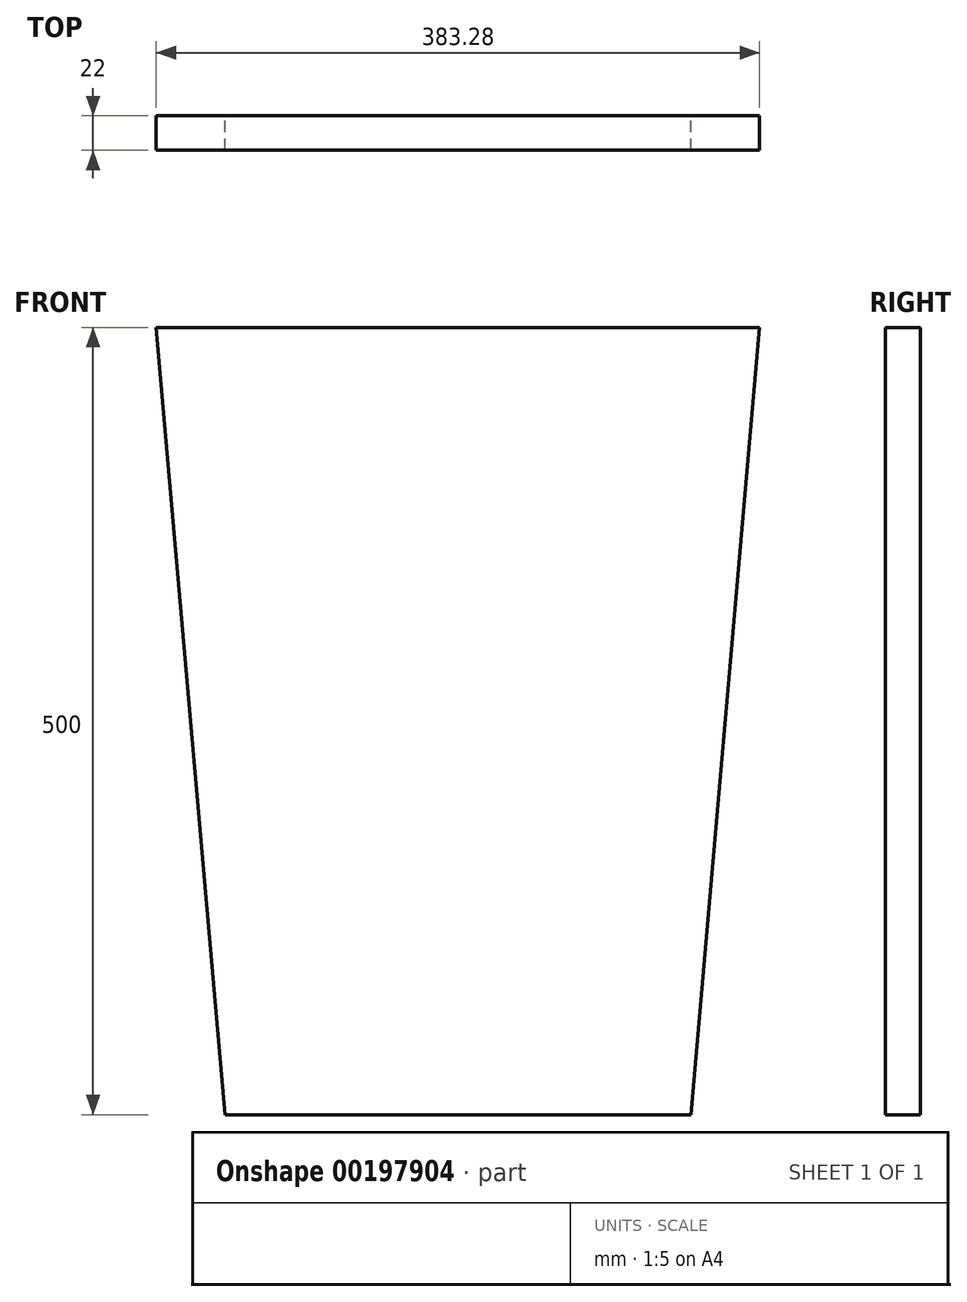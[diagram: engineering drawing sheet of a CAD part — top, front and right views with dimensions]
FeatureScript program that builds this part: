
annotation { "Feature Type Name" : "Feature", "Feature Type Description" : "" }
export const myFeature = defineFeature(function(context is Context, id is Id, definition is map)
    precondition{}
    {
        {
            var Q0;
            Q0=qCreatedBy(makeId("Front.planeOp"),FACE);
            var sketch = newSketch(context, id + "F0", { "sketchPlane" : qUnion([Q0])});
            skLineSegment(sketch, "E0", {"start": v(-191.64, 310.85) * mm, "end": v(-147.9, -189.15) * mm});
            skLineSegment(sketch, "E1", {"start": v(-147.9, -189.15) * mm, "end": v(147.9, -189.15) * mm});
            skLineSegment(sketch, "E2", {"start": v(147.9, -189.15) * mm, "end": v(191.64, 310.85) * mm});
            skLineSegment(sketch, "E3", {"start": v(191.64, 310.85) * mm, "end": v(-191.64, 310.85) * mm});
            skLineSegment(sketch, "E4", {"start": v(-150, -165.15) * mm, "end": v(150, -165.15) * mm});
            skSolve(sketch);
        }
        {
            var Q0;
            Q0 = qSketchRegion(id + "F0", true);
            extrude(context, id + "F1", {"entities" : qUnion([Q0]), "depth" : 22 * mm});
        }
    });
